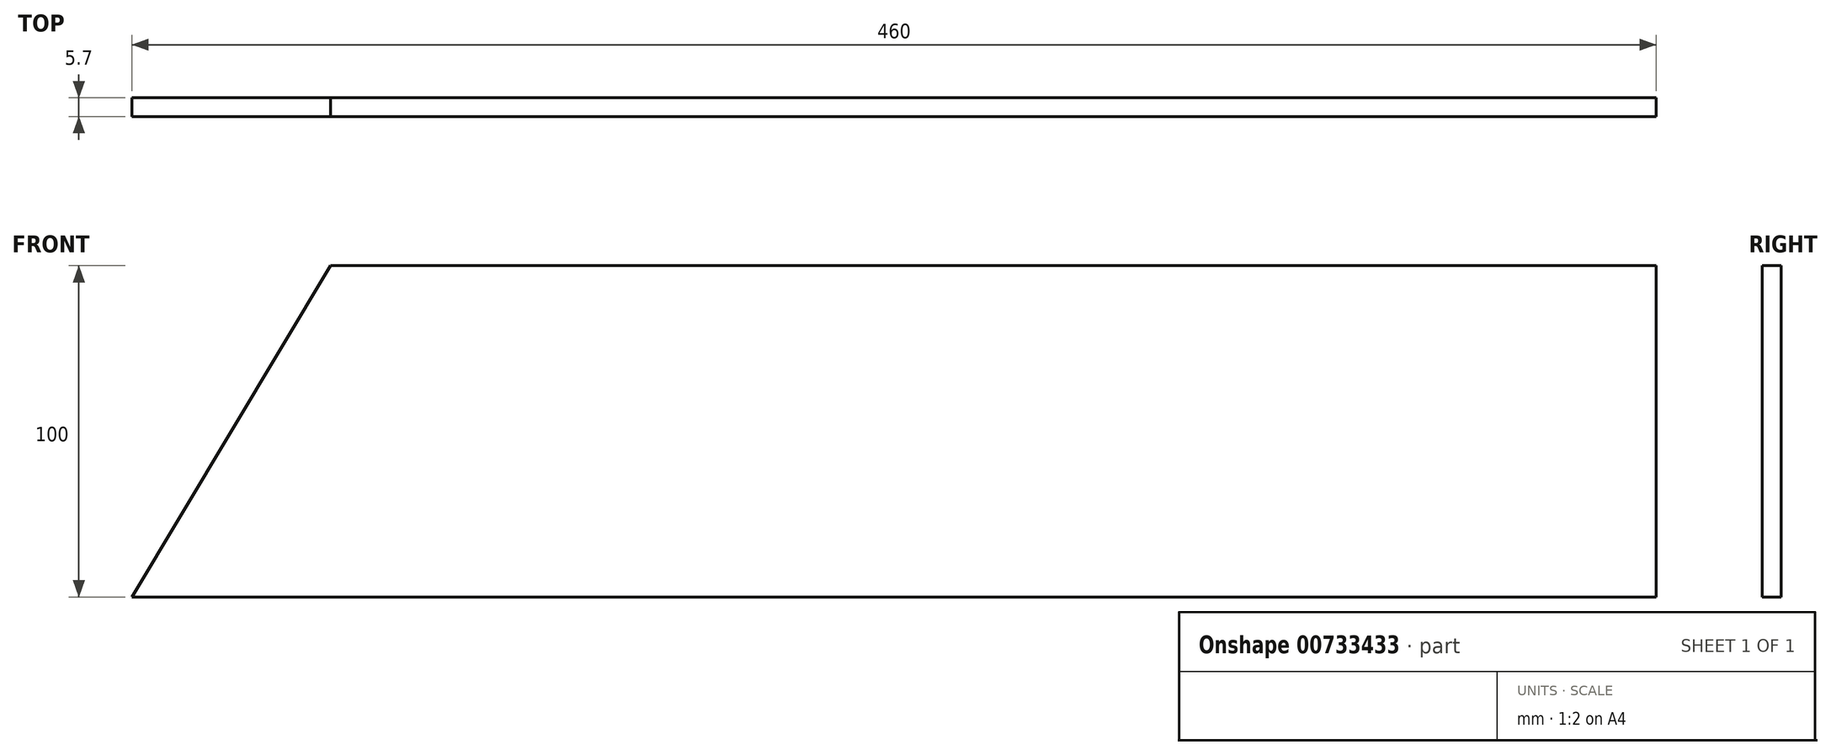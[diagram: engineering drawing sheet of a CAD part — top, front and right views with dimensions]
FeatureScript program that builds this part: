
annotation { "Feature Type Name" : "Feature", "Feature Type Description" : "" }
export const myFeature = defineFeature(function(context is Context, id is Id, definition is map)
    precondition{}
    {
        {
            var Q0;
            Q0=qCreatedBy(makeId("Front.planeOp"),FACE);
            var sketch = newSketch(context, id + "F0", { "sketchPlane" : qUnion([Q0])});
            skLineSegment(sketch, "E0.bottom", {"start": v(0, 0) * mm, "end": v(400, 0) * mm});
            skLineSegment(sketch, "E0.top", {"start": v(0, 100) * mm, "end": v(400, 100) * mm});
            skLineSegment(sketch, "E0.left", {"start": v(0, 0) * mm, "end": v(0, 100) * mm});
            skLineSegment(sketch, "E0.right", {"start": v(400, 0) * mm, "end": v(400, 100) * mm});
            skLineSegment(sketch, "E1", {"start": v(0, 100) * mm, "end": v(-60, 0) * mm});
            skLineSegment(sketch, "E2", {"start": v(-60, 0) * mm, "end": v(0, 0) * mm});
            skSolve(sketch);
        }
        {
            var Q0;
            Q0 = qSketchRegion(id + "F0", true);
            extrude(context, id + "F1", {"entities" : qUnion([Q0]), "depth" : 5.7 * mm, "offsetDistance" : 25 * mm});
        }
    });
